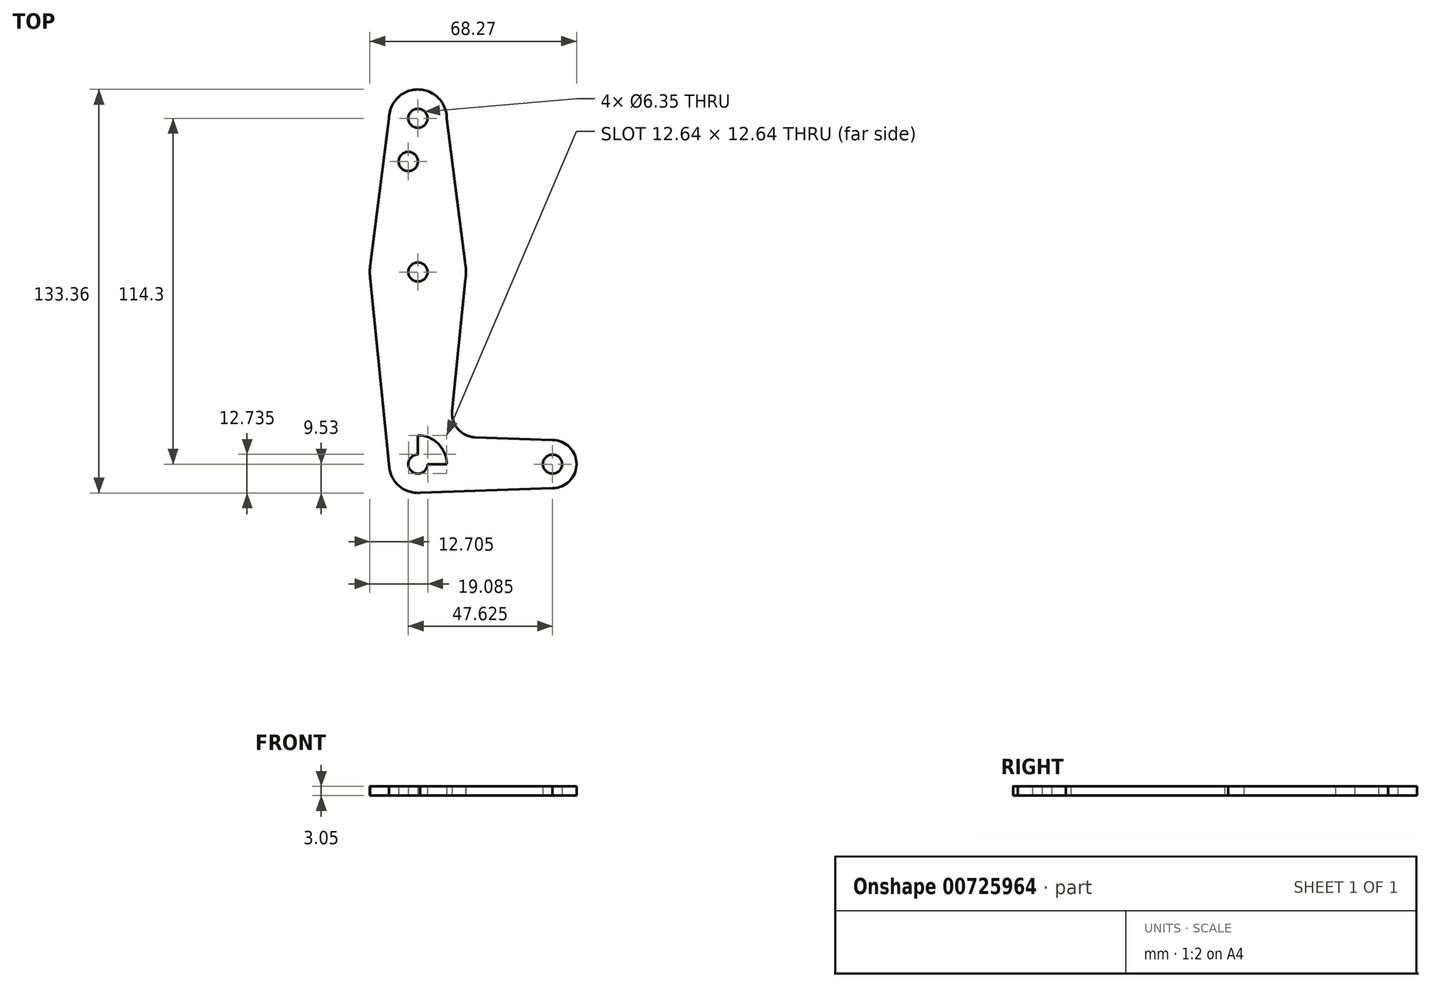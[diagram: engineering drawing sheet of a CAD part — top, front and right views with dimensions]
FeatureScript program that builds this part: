
annotation { "Feature Type Name" : "Feature", "Feature Type Description" : "" }
export const myFeature = defineFeature(function(context is Context, id is Id, definition is map)
    precondition{}
    {
        {
            var Q0;
            Q0=qCreatedBy(makeId("Top.planeOp"),FACE);
            var sketch = newSketch(context, id + "F0", { "sketchPlane" : qUnion([Q0])});
            skLineSegment(sketch, "E0", {"start": v(0, 0) * mm, "end": v(0, 114.3) * mm});
            skLineSegment(sketch, "E1", {"start": v(0, 0) * mm, "end": v(44.45, 0) * mm});
            skCircle(sketch, "E2", {"center": v(0, 0) * mm, "radius": 9.52 * mm});
            skCircle(sketch, "E3", {"center": v(44.45, 0) * mm, "radius": 7.94 * mm});
            skCircle(sketch, "E4", {"center": v(0, 63.5) * mm, "radius": 15.88 * mm});
            skCircle(sketch, "E5", {"center": v(0, 114.3) * mm, "radius": 9.53 * mm});
            skLineSegment(sketch, "E6", {"start": v(0, 63.5) * mm, "end": v(0, 0) * mm});
            skLineSegment(sketch, "E7", {"start": v(-9.52, 114.27) * mm, "end": v(-15.75, 65.5) * mm});
            skLineSegment(sketch, "E8", {"start": v(-15.75, 65.5) * mm, "end": v(-15.75, 61.5) * mm});
            skLineSegment(sketch, "E9", {"start": v(-15.75, 61.5) * mm, "end": v(-9.57, 0) * mm});
            skLineSegment(sketch, "E10", {"start": v(11.3, 17.6) * mm, "end": v(15.75, 61.5) * mm});
            skLineSegment(sketch, "E11", {"start": v(15.75, 61.5) * mm, "end": v(15.75, 65.47) * mm});
            skLineSegment(sketch, "E12", {"start": v(15.75, 65.47) * mm, "end": v(9.53, 114.3) * mm});
            skLineSegment(sketch, "E13", {"start": v(0, 0) * mm, "end": v(-9.57, 0) * mm});
            skLineSegment(sketch, "E14", {"start": v(0, 9.53) * mm, "end": v(0, -9.52) * mm});
            skLineSegment(sketch, "E15", {"start": v(0, -9.52) * mm, "end": v(44.45, -7.94) * mm});
            skLineSegment(sketch, "E16", {"start": v(44.45, 0) * mm, "end": v(44.45, -7.94) * mm});
            skCircle(sketch, "E17", {"center": v(0, 114.3) * mm, "radius": 3.18 * mm});
            skCircle(sketch, "E18", {"center": v(0, 63.5) * mm, "radius": 3.18 * mm});
            skCircle(sketch, "E19", {"center": v(44.45, 0) * mm, "radius": 3.18 * mm});
            skCircle(sketch, "E20", {"center": v(-3.18, 100.03) * mm, "radius": 3.18 * mm});
            skLineSegment(sketch, "E21", {"start": v(9.53, 0) * mm, "end": v(9.53, 0) * mm});
            skLineSegment(sketch, "E22", {"start": v(0, 9.53) * mm, "end": v(0, 9.53) * mm});
            skLineSegment(sketch, "E23", {"start": v(0, 9.53) * mm, "end": v(0, 3.2) * mm});
            skLineSegment(sketch, "E24", {"start": v(18.93, 8.85) * mm, "end": v(44.45, 7.94) * mm});
            skArc(sketch, "E25.filletArc", {"start": v(11.3, 17.6) * mm, "mid": v(13.22, 11.57) * mm, "end": v(18.93, 8.85) * mm});
            skCircle(sketch, "E26", {"center": v(0, 0) * mm, "radius": 3.18 * mm});
            skLineSegment(sketch, "E27", {"start": v(0, 9.53) * mm, "end": v(0, 0) * mm});
            skLineSegment(sketch, "E28", {"start": v(9.53, 0) * mm, "end": v(3.18, 0) * mm});
            skLineSegment(sketch, "E29", {"start": v(3.18, 0) * mm, "end": v(0, 0) * mm});
            skLineSegment(sketch, "E30", {"start": v(0, 3.2) * mm, "end": v(0, 9.53) * mm});
            skSolve(sketch);
        }
        {
            var Q0;
            Q0 = qSketchRegion(id + "F0", true);
            var Q1;
            {var subQ0=sQuery(id+"F0.wireOp",EDGE,"E28");Q1=makeQuery(id+"F0.imprint","IMPRINT",FACE,{"disambiguationData":[TD([[makeQuery(id+"F0.imprint","IMPRINT",EDGE,{"derivedFrom":subQ0}),-1.0]])]});}
            extrude(context, id + "F1", {"entities" : qUnion([Q0, Q1]), "depth" : 3.05 * mm, "offsetDistance" : 25.4 * mm});
        }
    });
